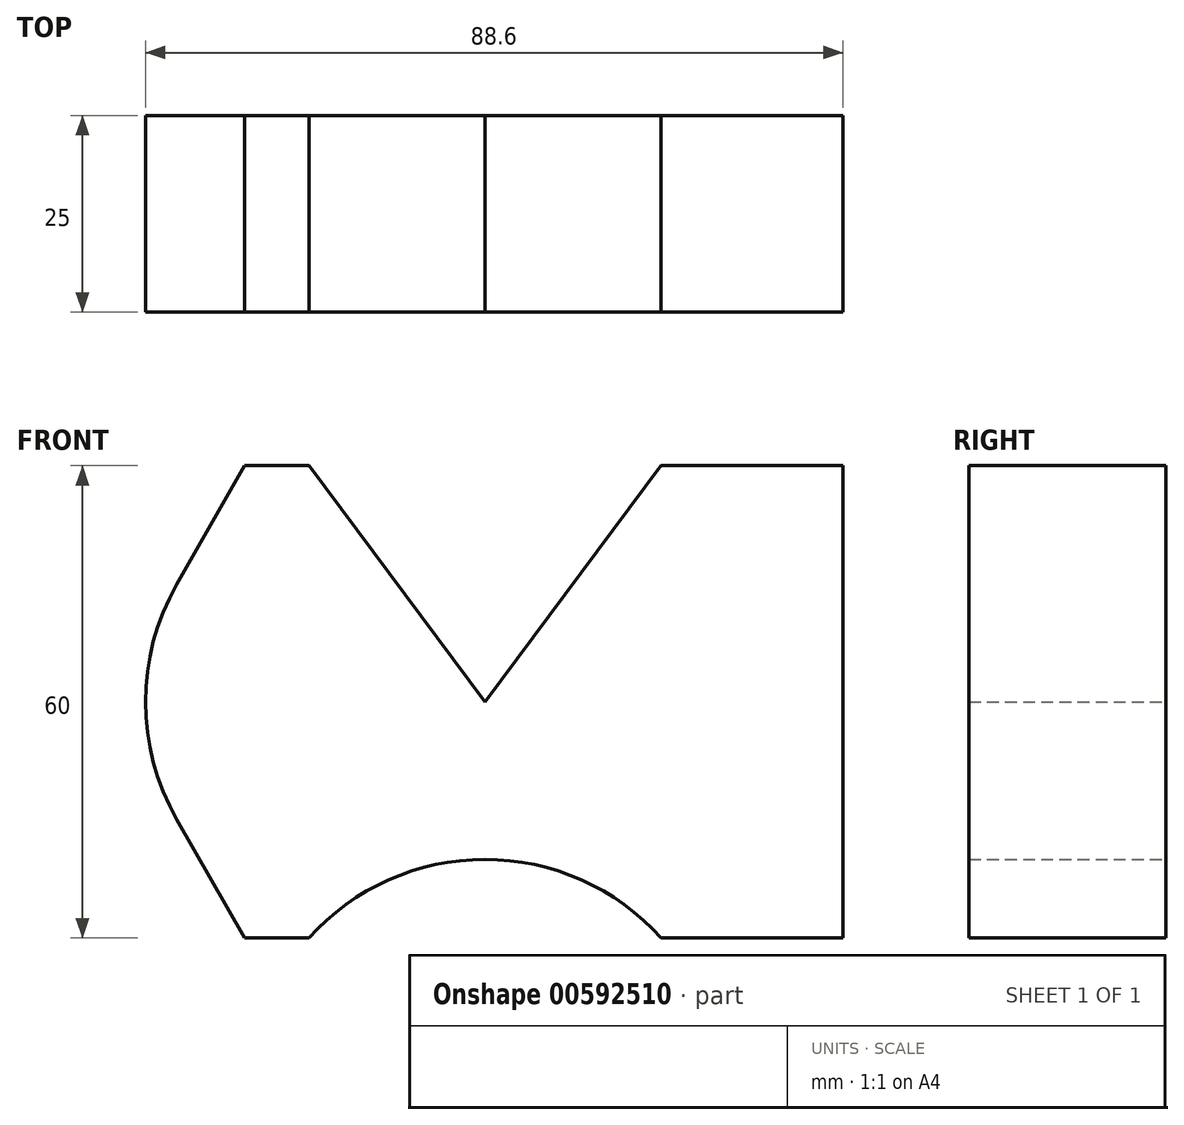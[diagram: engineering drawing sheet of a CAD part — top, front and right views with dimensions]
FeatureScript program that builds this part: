
annotation { "Feature Type Name" : "Feature", "Feature Type Description" : "" }
export const myFeature = defineFeature(function(context is Context, id is Id, definition is map)
    precondition{}
    {
        {
            var Q0;
            Q0=qCreatedBy(makeId("Front.planeOp"),FACE);
            var sketch = newSketch(context, id + "F0", { "sketchPlane" : qUnion([Q0])});
            skLineSegment(sketch, "E0", {"start": v(0, 0) * mm, "end": v(22.36, 30) * mm});
            skLineSegment(sketch, "E1", {"start": v(22.36, 30) * mm, "end": v(45.48, 30) * mm});
            skLineSegment(sketch, "E2", {"start": v(45.48, 30) * mm, "end": v(45.48, -30) * mm});
            skLineSegment(sketch, "E3", {"start": v(45.48, -30) * mm, "end": v(22.36, -30) * mm});
            skLineSegment(sketch, "E4", {"start": v(-22.36, -30) * mm, "end": v(-30.51, -30) * mm});
            skLineSegment(sketch, "E5", {"start": v(-30.51, -30) * mm, "end": v(-39.15, -14.9) * mm});
            skLineSegment(sketch, "E6", {"start": v(0, 0) * mm, "end": v(-22.36, 30) * mm});
            skLineSegment(sketch, "E7", {"start": v(-22.36, 30) * mm, "end": v(-30.51, 30) * mm});
            skLineSegment(sketch, "E8", {"start": v(-30.51, 30) * mm, "end": v(-39.15, 14.9) * mm});
            skArc(sketch, "E9", {"start": v(-39.15, 14.9) * mm, "mid": v(-43.12, 0) * mm, "end": v(-39.15, -14.9) * mm});
            skArc(sketch, "E10", {"start": v(22.36, -30) * mm, "mid": v(0, -20) * mm, "end": v(-22.36, -30) * mm});
            skLineSegment(sketch, "E11", {"start": v(-30.51, 30) * mm, "end": v(-30.51, -30) * mm, "construction": true});
            skSolve(sketch);
        }
        {
            var Q0;
            Q0=makeQuery(id+"F0.imprint","IMPRINT",FACE,{"disambiguationData":[TD([[makeQuery(id+"F0.imprint","IMPRINT",EDGE,{"derivedFrom":sQuery(id+"F0.wireOp",EDGE,"E0")}),-1.0]])]});
            extrude(context, id + "F1", {"entities" : qUnion([Q0]), "depth" : 25 * mm, "offsetDistance" : 25 * mm});
        }
    });
